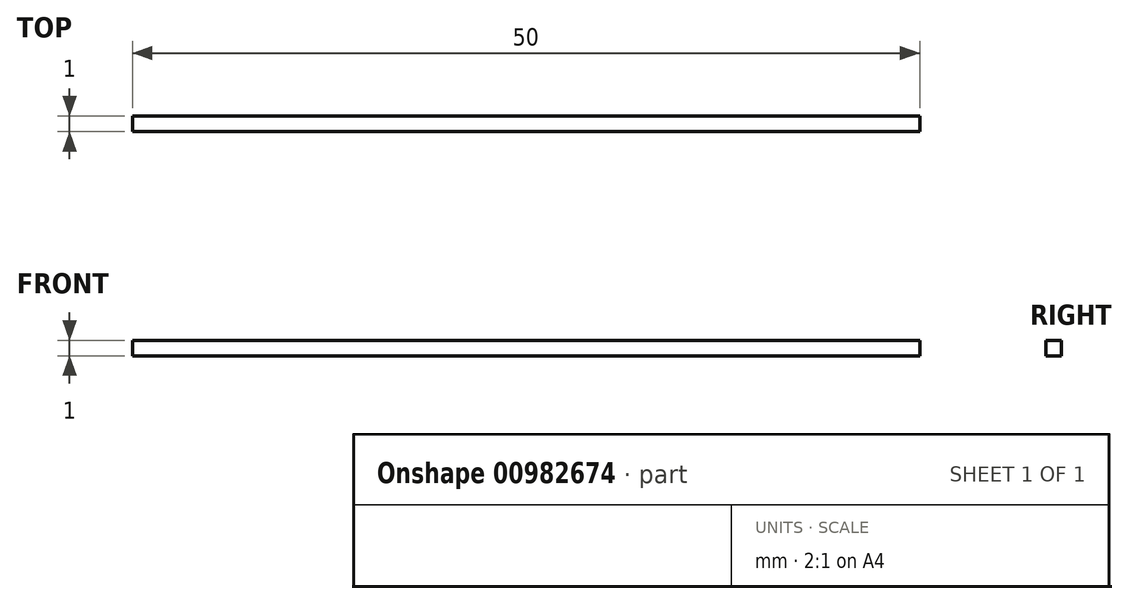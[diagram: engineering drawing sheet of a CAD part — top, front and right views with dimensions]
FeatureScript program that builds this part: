
annotation { "Feature Type Name" : "Feature", "Feature Type Description" : "" }
export const myFeature = defineFeature(function(context is Context, id is Id, definition is map)
    precondition{}
    {
        {
            var Q0;
            Q0=qCreatedBy(makeId("Front.planeOp"),FACE);
            var sketch = newSketch(context, id + "F0", { "sketchPlane" : qUnion([Q0])});
            skLineSegment(sketch, "E0.bottom", {"start": v(0, 0) * mm, "end": v(50, 0) * mm});
            skLineSegment(sketch, "E0.top", {"start": v(0, 1) * mm, "end": v(50, 1) * mm});
            skLineSegment(sketch, "E0.left", {"start": v(0, 0) * mm, "end": v(0, 1) * mm});
            skLineSegment(sketch, "E0.right", {"start": v(50, 0) * mm, "end": v(50, 1) * mm});
            skSolve(sketch);
        }
        {
            var Q0;
            Q0 = qSketchRegion(id + "F0", true);
            extrude(context, id + "F1", {"entities" : qUnion([Q0]), "depth" : 1 * mm, "offsetDistance" : 25 * mm});
        }
    });
